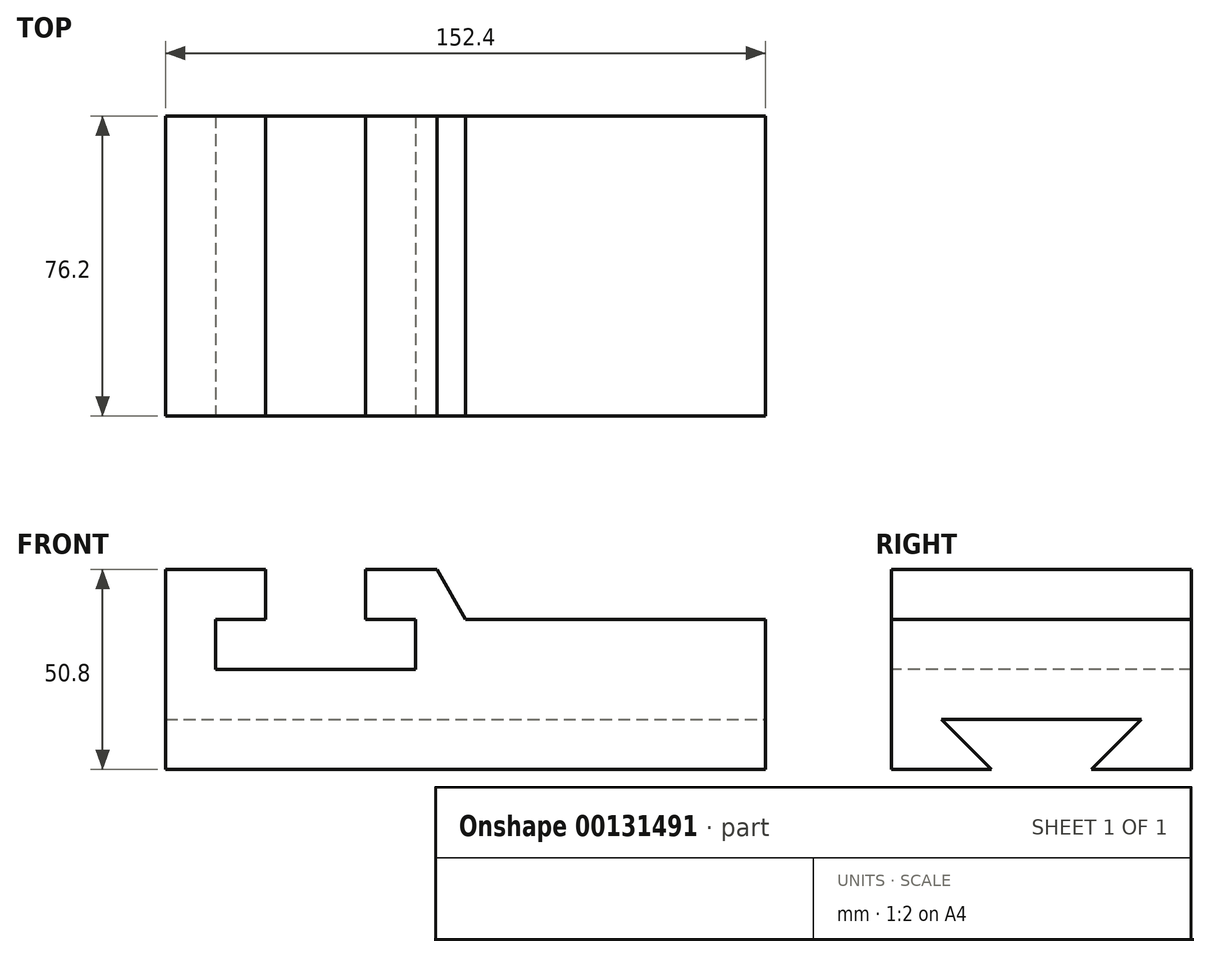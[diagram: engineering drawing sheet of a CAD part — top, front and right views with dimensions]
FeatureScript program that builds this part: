
annotation { "Feature Type Name" : "Feature", "Feature Type Description" : "" }
export const myFeature = defineFeature(function(context is Context, id is Id, definition is map)
    precondition{}
    {
        {
            var Q0;
            Q0=qCreatedBy(makeId("Top.planeOp"),FACE);
            var sketch = newSketch(context, id + "F0", { "sketchPlane" : qUnion([Q0])});
            skLineSegment(sketch, "E0.bottom", {"start": v(-76.2, 38.1) * mm, "end": v(76.2, 38.1) * mm});
            skLineSegment(sketch, "E0.top", {"start": v(-76.2, -38.1) * mm, "end": v(76.2, -38.1) * mm});
            skLineSegment(sketch, "E0.left", {"start": v(-76.2, 38.1) * mm, "end": v(-76.2, -38.1) * mm});
            skLineSegment(sketch, "E0.right", {"start": v(76.2, 38.1) * mm, "end": v(76.2, -38.1) * mm});
            skPoint(sketch, "E0.middle", {"position": v(0, 0) * mm});
            skSolve(sketch);
        }
        {
            var Q0;
            Q0 = qSketchRegion(id + "F0", true);
            extrude(context, id + "F1", {"entities" : qUnion([Q0]), "depth" : 50.8 * mm});
        }
        {
            var Q0;
            Q0=makeQuery(id+"F1.opExtrude","SWEPT_FACE",FACE,{"disambiguationData":[OSD([sQuery(id+"F0.wireOp",EDGE,"E0.right")])]});
            var sketch = newSketch(context, id + "F2", { "sketchPlane" : qUnion([Q0])});
            skLineSegment(sketch, "E1", {"start": v(-38.1, 0) * mm, "end": v(-25.4, 0) * mm});
            skLineSegment(sketch, "E2", {"start": v(-25.4, 0) * mm, "end": v(-25.4, 12.7) * mm});
            skLineSegment(sketch, "E3", {"start": v(-25.4, 0) * mm, "end": v(-12.7, 0) * mm});
            skLineSegment(sketch, "E4", {"start": v(38.1, 0) * mm, "end": v(25.4, 0) * mm});
            skLineSegment(sketch, "E5", {"start": v(25.4, 0) * mm, "end": v(25.4, 12.7) * mm});
            skLineSegment(sketch, "E6", {"start": v(25.4, 0) * mm, "end": v(12.7, 0) * mm});
            skLineSegment(sketch, "E7", {"start": v(-25.4, 12.7) * mm, "end": v(-12.7, 0) * mm});
            skLineSegment(sketch, "E8", {"start": v(-12.7, 0) * mm, "end": v(12.7, 0) * mm});
            skLineSegment(sketch, "E9", {"start": v(12.7, 0) * mm, "end": v(25.4, 12.7) * mm});
            skLineSegment(sketch, "E10", {"start": v(25.4, 12.7) * mm, "end": v(-25.4, 12.7) * mm});
            skSolve(sketch);
        }
        {
            var Q0;
            Q0=makeQuery(id+"F2.imprint","IMPRINT",FACE,{"disambiguationData":[TD([[makeQuery(id+"F2.imprint","IMPRINT",EDGE,{"derivedFrom":sQuery(id+"F2.wireOp",EDGE,"E7")}),1.0]])]});
            extrude(context, id + "F3", {"entities" : qUnion([Q0]), "operationType" : NewBodyOperationType.REMOVE, "endBound" : BoundingType.THROUGH_ALL, "oppositeDirection" : true, "depth" : 25.4 * mm});
        }
        {
            var Q0;
            Q0=makeQuery(id+"F1.opExtrude","SWEPT_FACE",FACE,{"disambiguationData":[OSD([sQuery(id+"F0.wireOp",EDGE,"E0.top")])]});
            var sketch = newSketch(context, id + "F4", { "sketchPlane" : qUnion([Q0])});
            skLineSegment(sketch, "E11", {"start": v(-76.2, 50.8) * mm, "end": v(-76.2, 25.4) * mm});
            skLineSegment(sketch, "E12", {"start": v(-76.2, 25.4) * mm, "end": v(-63.5, 25.4) * mm});
            skLineSegment(sketch, "E13", {"start": v(-63.5, 25.4) * mm, "end": v(-63.5, 38.1) * mm});
            skLineSegment(sketch, "E14", {"start": v(-63.5, 38.1) * mm, "end": v(-50.8, 38.1) * mm});
            skLineSegment(sketch, "E15", {"start": v(-50.8, 38.1) * mm, "end": v(-50.8, 50.8) * mm});
            skLineSegment(sketch, "E16", {"start": v(-63.5, 25.4) * mm, "end": v(-12.7, 25.4) * mm});
            skLineSegment(sketch, "E17", {"start": v(-12.7, 25.4) * mm, "end": v(-12.7, 38.1) * mm});
            skLineSegment(sketch, "E18", {"start": v(-12.7, 38.1) * mm, "end": v(-25.4, 38.1) * mm});
            skLineSegment(sketch, "E19", {"start": v(-25.4, 38.1) * mm, "end": v(-25.4, 50.8) * mm});
            skLineSegment(sketch, "E20", {"start": v(-50.8, 50.8) * mm, "end": v(-25.4, 50.8) * mm});
            skSolve(sketch);
        }
        {
            var Q0;
            Q0=makeQuery(id+"F4.imprint","IMPRINT",FACE,{"disambiguationData":[TD([[makeQuery(id+"F4.imprint","IMPRINT",EDGE,{"derivedFrom":sQuery(id+"F4.wireOp",EDGE,"E13")}),-1.0]])]});
            extrude(context, id + "F5", {"entities" : qUnion([Q0]), "operationType" : NewBodyOperationType.REMOVE, "endBound" : BoundingType.THROUGH_ALL, "oppositeDirection" : true, "depth" : 25.4 * mm});
        }
        {
            var Q0;
            Q0=makeQuery(id+"F1.opExtrude","SWEPT_FACE",FACE,{"disambiguationData":[OSD([sQuery(id+"F0.wireOp",EDGE,"E0.top")])]});
            var sketch = newSketch(context, id + "F6", { "sketchPlane" : qUnion([Q0])});
            skLineSegment(sketch, "E21", {"start": v(76.2, 50.8) * mm, "end": v(76.2, 38.1) * mm});
            skLineSegment(sketch, "E22", {"start": v(76.2, 38.1) * mm, "end": v(0, 38.1) * mm});
            skLineSegment(sketch, "E23", {"start": v(0, 38.1) * mm, "end": v(0, 50.8) * mm});
            skLineSegment(sketch, "E24", {"start": v(-0.92, 50.85) * mm, "end": v(-7.27, 50.8) * mm});
            skLineSegment(sketch, "E25", {"start": v(-7.27, 50.8) * mm, "end": v(0, 38.1) * mm});
            skSolve(sketch);
        }
        {
            var Q0;
            {var subQ0=sQuery(id+"F6.wireOp",EDGE,"E21");Q0=makeQuery(id+"F6.imprint","IMPRINT",FACE,{"disambiguationData":[TD([[makeQuery(id+"F6.imprint","IMPRINT",EDGE,{"derivedFrom":subQ0}),-1.0]])]});}
            var Q1;
            {var subQ0=sQuery(id+"F6.wireOp",EDGE,"E23");Q1=makeQuery(id+"F6.imprint","IMPRINT",FACE,{"disambiguationData":[TD([[makeQuery(id+"F6.imprint","IMPRINT",EDGE,{"derivedFrom":subQ0}),1.0]])]});}
            extrude(context, id + "F7", {"entities" : qUnion([Q0, Q1]), "operationType" : NewBodyOperationType.REMOVE, "endBound" : BoundingType.THROUGH_ALL, "oppositeDirection" : true, "depth" : 25.4 * mm});
        }
    });
